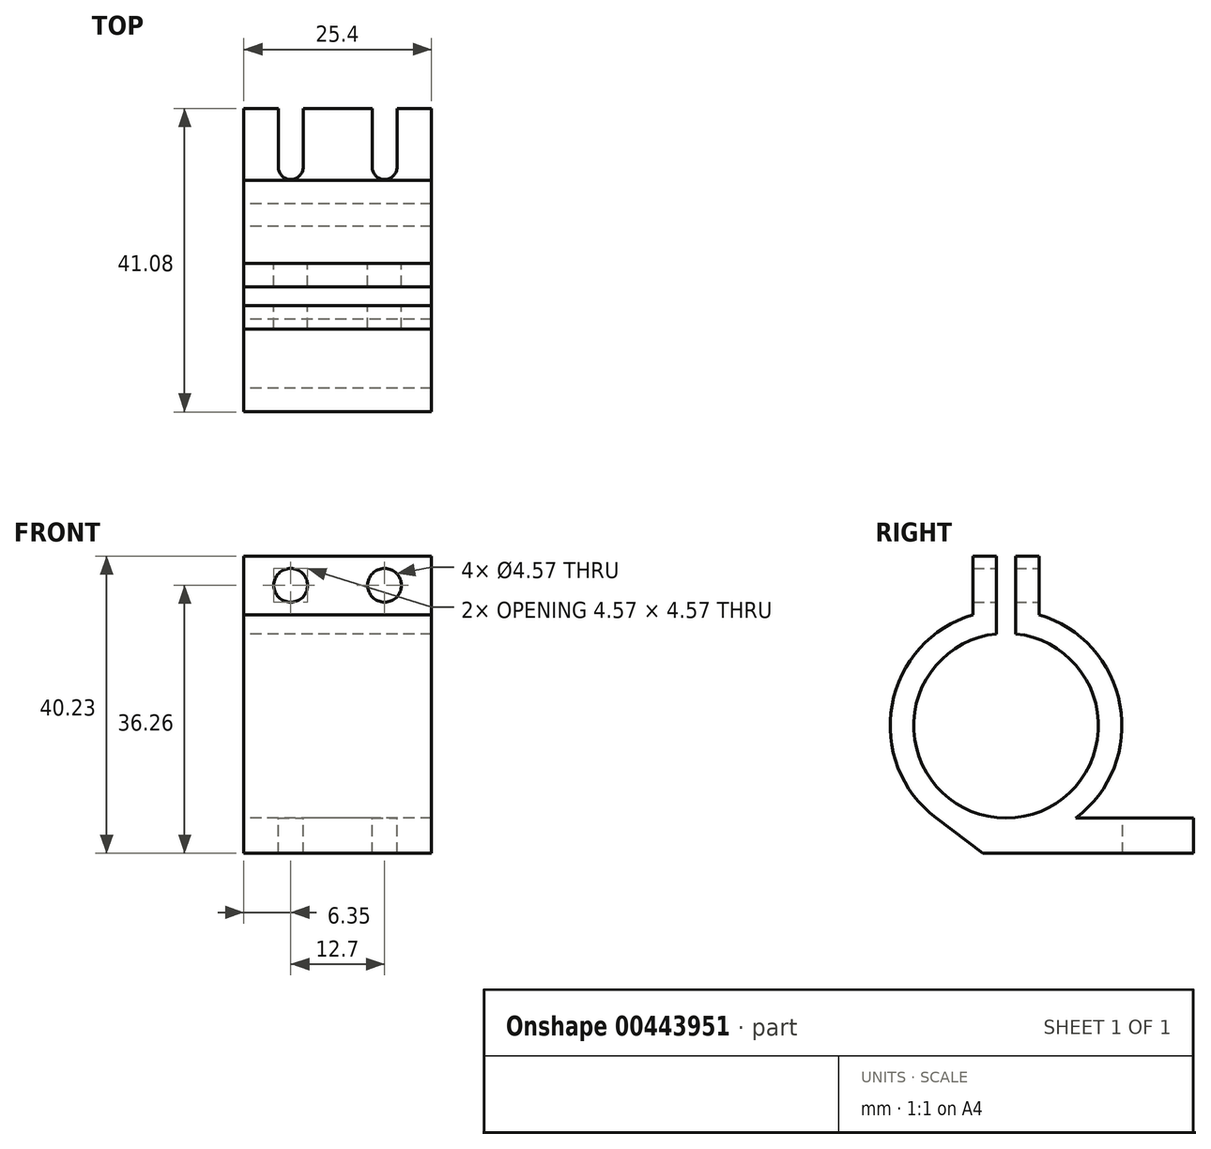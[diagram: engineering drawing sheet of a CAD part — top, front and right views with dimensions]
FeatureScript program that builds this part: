
annotation { "Feature Type Name" : "Feature", "Feature Type Description" : "" }
export const myFeature = defineFeature(function(context is Context, id is Id, definition is map)
    precondition{}
    {
        {
            var Q0;
            Q0=qCreatedBy(makeId("Right.planeOp"),FACE);
            var sketch = newSketch(context, id + "F0", { "sketchPlane" : qUnion([Q0])});
            skArc(sketch, "E0", {"start": v(-1.27, 12.44) * mm, "mid": v(0, -12.5) * mm, "end": v(1.27, 12.44) * mm});
            skLineSegment(sketch, "E1", {"start": v(-1.27, 12.44) * mm, "end": v(-1.27, 22.97) * mm});
            skLineSegment(sketch, "E2", {"start": v(-1.27, 22.97) * mm, "end": v(-4.45, 22.97) * mm});
            skLineSegment(sketch, "E3", {"start": v(-4.45, 22.97) * mm, "end": v(-4.45, 15.03) * mm});
            skLineSegment(sketch, "E4", {"start": v(1.27, 12.44) * mm, "end": v(1.27, 22.97) * mm});
            skLineSegment(sketch, "E5", {"start": v(1.27, 22.97) * mm, "end": v(4.45, 22.97) * mm});
            skLineSegment(sketch, "E6", {"start": v(4.45, 22.97) * mm, "end": v(4.45, 15.03) * mm});
            skArc(sketch, "E7", {"start": v(-4.45, 15.03) * mm, "mid": v(-15.42, 2.8) * mm, "end": v(-9.46, -12.5) * mm});
            skLineSegment(sketch, "E8", {"start": v(-9.46, -12.5) * mm, "end": v(-25.4, -12.5) * mm});
            skLineSegment(sketch, "E9", {"start": v(-25.4, -12.5) * mm, "end": v(-25.4, -17.26) * mm});
            skLineSegment(sketch, "E10", {"start": v(-25.4, -17.26) * mm, "end": v(25.4, -17.26) * mm});
            skLineSegment(sketch, "E11", {"start": v(25.4, -17.26) * mm, "end": v(25.4, -12.5) * mm});
            skLineSegment(sketch, "E12", {"start": v(25.4, -12.5) * mm, "end": v(9.46, -12.5) * mm});
            skArc(sketch, "E13", {"start": v(4.45, 15.03) * mm, "mid": v(15.42, 2.8) * mm, "end": v(9.46, -12.5) * mm});
            skSolve(sketch);
        }
        {
            var Q0;
            Q0=qSketchRegion(id+"F0",true);
            extrude(context, id + "F1", {"entities" : qUnion([Q0]), "depth" : 25.4 * mm});
        }
        {
            var Q0;
            Q0=makeQuery(id+"F1.opExtrude","CAP_FACE",FACE,{"disambiguationData":[OSD([sQuery(id+"F0.wireOp",EDGE,"E0"),sQuery(id+"F0.wireOp",EDGE,"E1"),sQuery(id+"F0.wireOp",EDGE,"E2"),sQuery(id+"F0.wireOp",EDGE,"E3"),sQuery(id+"F0.wireOp",EDGE,"E4"),sQuery(id+"F0.wireOp",EDGE,"E5"),sQuery(id+"F0.wireOp",EDGE,"E6"),sQuery(id+"F0.wireOp",EDGE,"E7"),sQuery(id+"F0.wireOp",EDGE,"E8"),sQuery(id+"F0.wireOp",EDGE,"E9"),sQuery(id+"F0.wireOp",EDGE,"E10"),sQuery(id+"F0.wireOp",EDGE,"E11"),sQuery(id+"F0.wireOp",EDGE,"E12"),sQuery(id+"F0.wireOp",EDGE,"E13")])],"isStart":true});
            var sketch = newSketch(context, id + "F2", { "sketchPlane" : qUnion([Q0])});
            skLineSegment(sketch, "E14", {"start": v(9.46, -12.5) * mm, "end": v(3.16, -17.26) * mm});
            skLineSegment(sketch, "E15", {"start": v(3.16, -17.26) * mm, "end": v(25.4, -17.26) * mm});
            skLineSegment(sketch, "E16", {"start": v(25.4, -17.26) * mm, "end": v(25.4, -12.5) * mm});
            skLineSegment(sketch, "E17", {"start": v(25.4, -12.5) * mm, "end": v(9.46, -12.5) * mm});
            skSolve(sketch);
        }
        {
            var Q0;
            Q0=makeQuery(id+"F2.imprint","IMPRINT",FACE,{"disambiguationData":[TD([[makeQuery(id+"F2.imprint","IMPRINT",EDGE,{"derivedFrom":sQuery(id+"F2.wireOp",EDGE,"E14")}),1.0]])]});
            extrude(context, id + "F3", {"entities" : qUnion([Q0]), "operationType" : NewBodyOperationType.REMOVE, "endBound" : BoundingType.THROUGH_ALL, "oppositeDirection" : true, "depth" : 25.4 * mm});
        }
        {
            var Q0;
            Q0=makeQuery(id+"F1.opExtrude","SWEPT_FACE",FACE,{"disambiguationData":[OSD([sQuery(id+"F0.wireOp",EDGE,"E12")])]});
            var sketch = newSketch(context, id + "F4", { "sketchPlane" : qUnion([Q0])});
            skLineSegment(sketch, "E18", {"start": v(6.35, 17.46) * mm, "end": v(19.05, 17.46) * mm, "construction": true});
            skLineSegment(sketch, "E19", {"start": v(19.05, 17.46) * mm, "end": v(25.4, 17.46) * mm, "construction": true});
            skLineSegment(sketch, "E20", {"start": v(6.35, 17.46) * mm, "end": v(0, 17.46) * mm, "construction": true});
            skArc(sketch, "E21", {"start": v(4.66, 17.46) * mm, "mid": v(6.35, 15.77) * mm, "end": v(8.04, 17.46) * mm});
            skArc(sketch, "E22", {"start": v(17.36, 17.46) * mm, "mid": v(19.05, 15.77) * mm, "end": v(20.74, 17.46) * mm});
            skLineSegment(sketch, "E23", {"start": v(20.74, 17.46) * mm, "end": v(20.74, 25.4) * mm});
            skLineSegment(sketch, "E24", {"start": v(20.74, 25.4) * mm, "end": v(17.36, 25.4) * mm});
            skLineSegment(sketch, "E25", {"start": v(17.36, 25.4) * mm, "end": v(17.36, 17.46) * mm});
            skLineSegment(sketch, "E26", {"start": v(8.04, 17.46) * mm, "end": v(8.04, 25.4) * mm});
            skLineSegment(sketch, "E27", {"start": v(8.04, 25.4) * mm, "end": v(4.66, 25.4) * mm});
            skLineSegment(sketch, "E28", {"start": v(4.66, 25.4) * mm, "end": v(4.66, 17.46) * mm});
            skSolve(sketch);
        }
        {
            var Q0;
            Q0=qSketchRegion(id+"F4",true);
            extrude(context, id + "F5", {"entities" : qUnion([Q0]), "operationType" : NewBodyOperationType.REMOVE, "endBound" : BoundingType.UP_TO_NEXT, "oppositeDirection" : true, "depth" : 25.4 * mm});
        }
        {
            var Q0;
            Q0=makeQuery(id+"F1.opExtrude","SWEPT_FACE",FACE,{"disambiguationData":[OSD([sQuery(id+"F0.wireOp",EDGE,"E6")])]});
            var sketch = newSketch(context, id + "F6", { "sketchPlane" : qUnion([Q0])});
            skLineSegment(sketch, "E29", {"start": v(-25.4, 19) * mm, "end": v(-19.05, 19) * mm, "construction": true});
            skLineSegment(sketch, "E30", {"start": v(-19.05, 19) * mm, "end": v(-6.35, 19) * mm, "construction": true});
            skLineSegment(sketch, "E31", {"start": v(-6.35, 19) * mm, "end": v(0, 19) * mm, "construction": true});
            skCircle(sketch, "E32", {"center": v(-19.05, 19) * mm, "radius": 2.29 * mm});
            skCircle(sketch, "E33", {"center": v(-6.35, 19) * mm, "radius": 2.29 * mm});
            skSolve(sketch);
        }
        {
            var Q0;
            Q0=qSketchRegion(id+"F6",true);
            extrude(context, id + "F7", {"entities" : qUnion([Q0]), "operationType" : NewBodyOperationType.REMOVE, "endBound" : BoundingType.THROUGH_ALL, "oppositeDirection" : true, "depth" : 25.4 * mm});
        }
    });
